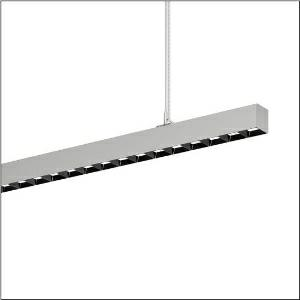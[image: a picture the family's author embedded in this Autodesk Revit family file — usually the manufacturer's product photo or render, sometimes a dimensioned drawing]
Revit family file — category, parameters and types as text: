
# Revit family: silica_r__21_51mx31dc4dsb_9913
name_source: partatom
category: Lighting Fixtures
units: mm (PartAtom-declared; Revit-internal decimal feet)

## family parameters
Cut with Voids When Loaded = No
Host = Face
Light Source = No
Part Type = Normal
Room Calculation Point = No
Round Connector Dimension = Use Diameter
Shared = No

## types (1)
- --- (1 x LED, 18230 lm, 105.9 W, 4000K)
    Apparent Load = 106 VA
    CIE Flux Codes = 87 99 100 59 100
    Color Rendering = 80
    Color Temperature = 4000K
    Default Elevation = 1800 mm
    Description = Silica® 21, office luminaire, primary light control with darklight reflector, of PMMA, black, CAT 2 (L<= 3000cd/m²), light emission: direct/indirect distribution, primary light characteristic: symmetric, installation type: suspended mounting, LED, rated luminous flux: 18.230lm, luminous efficacy: 172lm/W, light colour: 840, colour temperature: 4000K, with terminal, 3+2-pole, max. 2.5mm², mains connection: 220..240V, AC, 50/60Hz, rated input power: 105.9W, luminaire housing, of aluminium, metallic grey (RAL 9006), length: 3.004mm, width: 53mm, height: 53mm, protection rating (complete): IP20, insulation class (complete): insulation class I (protective earthing), certification: CE, permissible operating ambient temperature: 0..+35°C, standard: EN 50419, packaging unit: 1 piece
    Height = 53 mm
    Lamp = 1 x LED
    Lamp Light Flux = 18230 lm
    Lamp Power = 105.9 W
    Lamp count = 1
    Length = 3004 mm
    Luminous efficacy = 172 lm/W
    Manufacturer = Siteco
    ModVariant = No
    Model = 51MX31DC4DSB
    Mounting Place = Ceiling
    Mounting Type = Pendant
    Number of Poles = 1
    OnlyDefault = Yes
    Power Factor = 1
    Product Name = Silica® 21
    Product group = office luminaire | ceiling pendant
    ProductGroupID = 905
    Protection Class = Protection class I
    Protection Degree = IP 20
    RLX_Detail_Level = 1
    RlxData = <blob elided: 65545 chars, md5=f7ce9d80>
    Socket = socket
    Standby Power = 0 W
    System Light Flux = 18230 lm
    System Power = 106 W
    Type Comments = factory setting: luminous flux: 100 % | dim-lin: 254 | 367 mA
    Type Image = l_1251731.jpg
    URL = http://relux.com
    VarID = @adj_030035
    Voltage = 0 V
    Weight = 0.00 kg
    Width = 53 mm

## geometry (parser evidence)
native form markers: Blend x4, Sweep x13
no freeform markers — native parametric forms only
